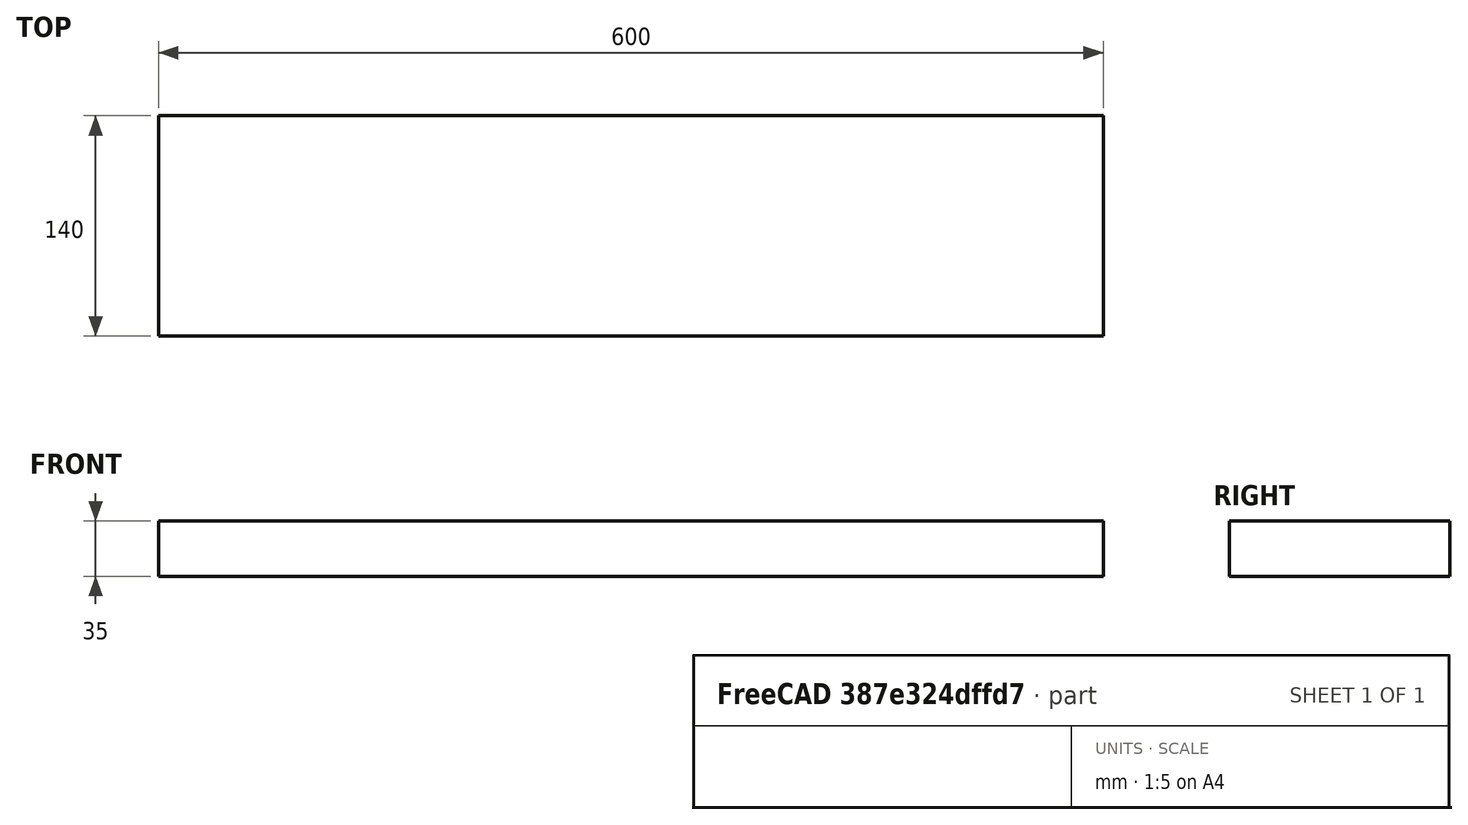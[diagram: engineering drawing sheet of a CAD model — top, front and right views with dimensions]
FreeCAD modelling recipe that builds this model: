
FCSTD DOCUMENT  (FreeCAD 0.18R4 (GitTag))
Label: lower_stretcher
License: All rights reserved
LicenseURL: http://en.wikipedia.org/wiki/All_rights_reserved
objects: Sketcher::SketchObject×1, PartDesign::Pad×1, PartDesign::Body×1
note: 4 computed .brp shape members not serialized (recipe doc carries the construction recipe); baked Part::Feature solids carry a one-line shape summary decoded from their .brp

FEATURE [Sketcher::SketchObject] Sketch
  MapMode = 5
  Placement = pos=(0,0,0) rot=(0.57735,0.57735,0.57735;2.0944rad)
  Support = -> [YZ_Plane]
  sketch-geometry (4):
    g0: LineSegment StartX=0 StartY=0 StartZ=0 EndX=-140 EndY=0 EndZ=0
    g1: LineSegment StartX=-140 StartY=0 StartZ=0 EndX=-140 EndY=35 EndZ=0
    g2: LineSegment StartX=-140 StartY=35 StartZ=0 EndX=0 EndY=35 EndZ=0
    g3: LineSegment StartX=0 StartY=35 StartZ=0 EndX=0 EndY=0 EndZ=0
  constraints (11):
    c: Coincident(g0,g1)
    c: Coincident(g1,g2)
    c: Coincident(g2,g3)
    c: Coincident(g3,g0)
    c: Horizontal(g0)
    c: Horizontal(g2)
    c: Vertical(g1)
    c: Vertical(g3)
    c: Coincident(g0,g-1)
    c: DistanceY(g3,g3) = 35
    c: DistanceX(g0,g0) = 140
FEATURE [PartDesign::Pad] Pad
  Length = 600
  Length2 = 100
  Placement = pos=(0,0,0) rot=(0.57735,0.57735,0.57735;2.0944rad)
  Profile = -> Sketch
  Type = 0
FEATURE [PartDesign::Body] Body
  Group = -> [Sketch,Pad]
  Origin = -> Origin
  Tip = -> Pad
